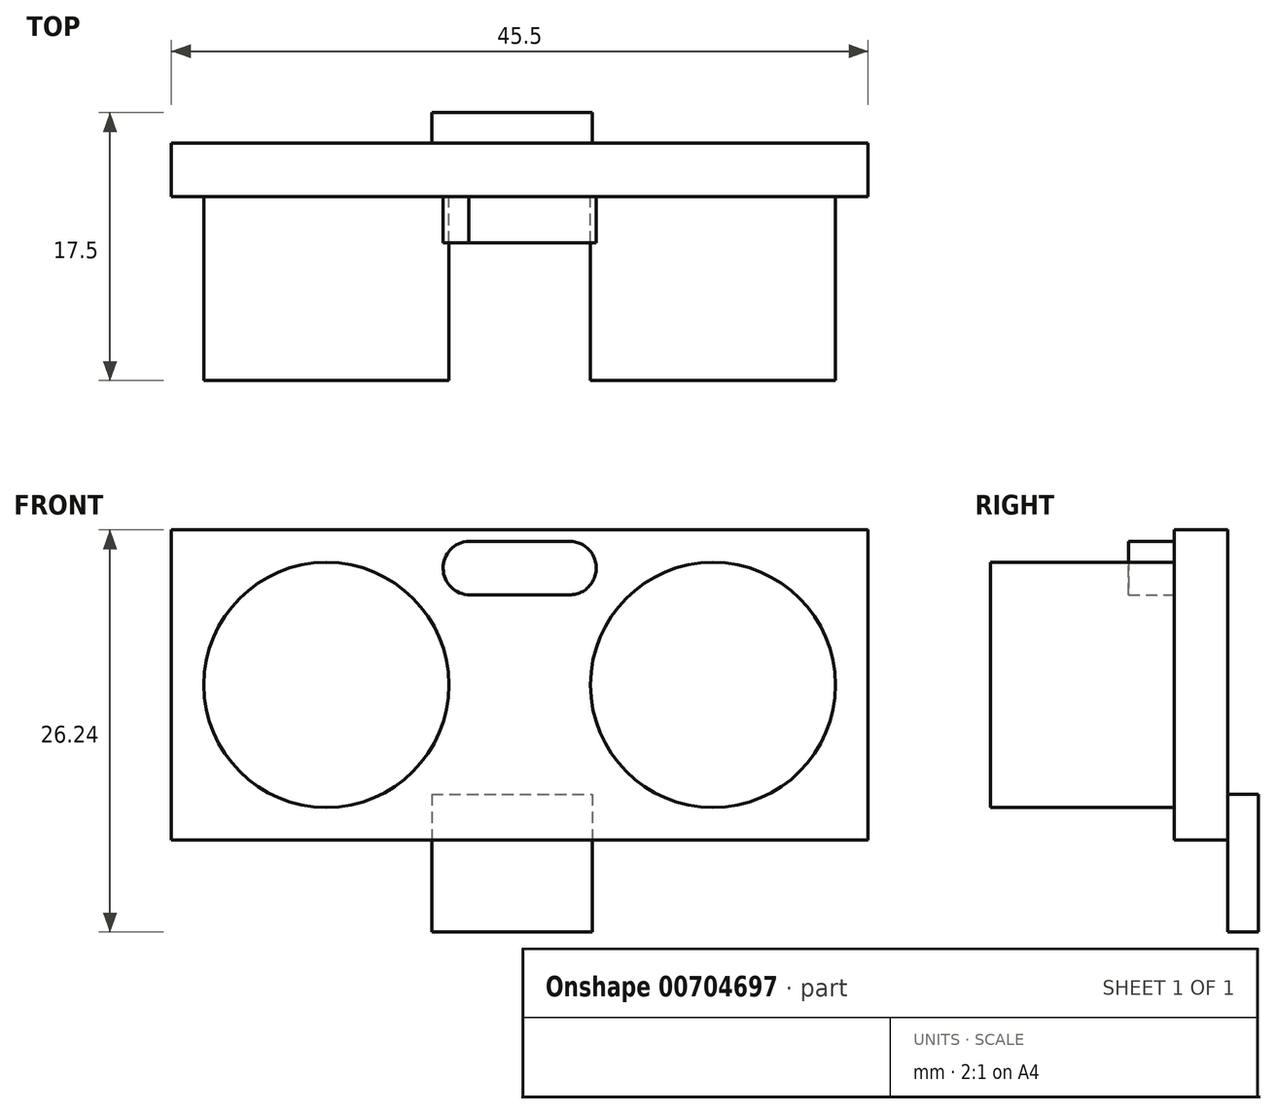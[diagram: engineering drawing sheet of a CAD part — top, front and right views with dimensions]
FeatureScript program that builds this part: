
annotation { "Feature Type Name" : "Feature", "Feature Type Description" : "" }
export const myFeature = defineFeature(function(context is Context, id is Id, definition is map)
    precondition{}
    {
        {
            var Q0;
            Q0=qCreatedBy(makeId("Front.planeOp"),FACE);
            var sketch = newSketch(context, id + "F0", { "sketchPlane" : qUnion([Q0])});
            skLineSegment(sketch, "E0.bottom", {"start": v(-22.75, 10.12) * mm, "end": v(22.75, 10.12) * mm});
            skLineSegment(sketch, "E0.top", {"start": v(-22.75, -10.13) * mm, "end": v(22.75, -10.12) * mm});
            skLineSegment(sketch, "E0.left", {"start": v(-22.75, 10.13) * mm, "end": v(-22.75, -10.12) * mm});
            skLineSegment(sketch, "E0.right", {"start": v(22.75, 10.13) * mm, "end": v(22.75, -10.12) * mm});
            skCircle(sketch, "E1", {"center": v(-12.62, 0) * mm, "radius": 8 * mm});
            skCircle(sketch, "E2", {"center": v(12.62, 0) * mm, "radius": 8 * mm});
            skLineSegment(sketch, "E3.bottom", {"start": v(-5.75, -7.12) * mm, "end": v(4.75, -7.12) * mm});
            skLineSegment(sketch, "E3.top", {"start": v(-5.75, -16.12) * mm, "end": v(4.75, -16.12) * mm});
            skLineSegment(sketch, "E3.left", {"start": v(-5.75, -7.12) * mm, "end": v(-5.75, -16.12) * mm});
            skLineSegment(sketch, "E3.right", {"start": v(4.75, -7.12) * mm, "end": v(4.75, -16.12) * mm});
            skCircle(sketch, "E4", {"center": v(-3.25, 7.63) * mm, "radius": 1.75 * mm});
            skCircle(sketch, "E5", {"center": v(3.25, 7.63) * mm, "radius": 1.75 * mm});
            skLineSegment(sketch, "E6", {"start": v(-3.25, 7.63) * mm, "end": v(3.25, 7.63) * mm});
            skLineSegment(sketch, "E7", {"start": v(-3.32, 9.38) * mm, "end": v(3.25, 9.38) * mm});
            skLineSegment(sketch, "E8", {"start": v(-3.25, 5.88) * mm, "end": v(3.25, 5.88) * mm});
            skSolve(sketch);
        }
        {
            var Q0;
            Q0=makeQuery(id+"F0.imprint","IMPRINT",FACE,{"disambiguationData":[TD([[makeQuery(id+"F0.imprint","IMPRINT",EDGE,{"derivedFrom":sQuery(id+"F0.wireOp",EDGE,"E0.bottom")}),-1.0]])]});
            var Q1;
            Q1=makeQuery(id+"F0.imprint","IMPRINT",FACE,{"disambiguationData":[TD([[makeQuery(id+"F0.imprint","IMPRINT",EDGE,{"derivedFrom":sQuery(id+"F0.wireOp",EDGE,"E1")}),1.0]])]});
            var Q2;
            Q2=makeQuery(id+"F0.imprint","IMPRINT",FACE,{"disambiguationData":[TD([[makeQuery(id+"F0.imprint","IMPRINT",EDGE,{"derivedFrom":sQuery(id+"F0.wireOp",EDGE,"E2")}),1.0]])]});
            var Q3;
            {var subQ5=sQuery(id+"F0.wireOp",EDGE,"E3.bottom");Q3=makeQuery(id+"F0.imprint","IMPRINT",FACE,{"disambiguationData":[TD([[makeQuery(id+"F0.imprint","IMPRINT",EDGE,{"derivedFrom":subQ5}),-1.0]])]});}
            extrude(context, id + "F1", {"entities" : qUnion([Q0, Q1, Q2, Q3]), "depth" : 3.5 * mm, "offsetDistance" : 25 * mm});
        }
        {
            var Q0;
            Q0=makeQuery(id+"F0.imprint","IMPRINT",FACE,{"disambiguationData":[TD([[makeQuery(id+"F0.imprint","IMPRINT",EDGE,{"derivedFrom":sQuery(id+"F0.wireOp",EDGE,"E1")}),1.0]])]});
            var Q1;
            Q1=makeQuery(id+"F0.imprint","IMPRINT",FACE,{"disambiguationData":[TD([[makeQuery(id+"F0.imprint","IMPRINT",EDGE,{"derivedFrom":sQuery(id+"F0.wireOp",EDGE,"E2")}),1.0]])]});
            extrude(context, id + "F2", {"entities" : qUnion([Q0, Q1]), "operationType" : NewBodyOperationType.ADD, "depth" : 15.5 * mm, "offsetDistance" : 25 * mm});
        }
        {
            var Q0;
            {var subQ0=sQuery(id+"F0.wireOp",EDGE,"E6");var subQ1=sQuery(id+"F0.wireOp",EDGE,"E4");var subQ2=makeQuery(id+"F0.imprint","INTERSECT",VERTEX,{"derivedFrom":[subQ1,subQ0]});Q0=makeQuery(id+"F0.imprint","IMPRINT",FACE,{"disambiguationData":[TD([[makeQuery(id+"F0.imprint","IMPRINT",EDGE,{"disambiguationData":[TD([[subQ2,-1.0]])],"derivedFrom":subQ1}),-1.0]])]});}
            var Q1;
            {var subQ3=sQuery(id+"F0.wireOp",EDGE,"E8");Q1=makeQuery(id+"F0.imprint","IMPRINT",FACE,{"disambiguationData":[TD([[makeQuery(id+"F0.imprint","IMPRINT",EDGE,{"derivedFrom":subQ3}),1.0]])]});}
            var Q2;
            {var subQ0=sQuery(id+"F0.wireOp",EDGE,"E4");var subQ1=makeQuery(id+"F0.imprint","INTERSECT",VERTEX,{"derivedFrom":[subQ0,sQuery(id+"F0.wireOp",EDGE,"E6")]});Q2=makeQuery(id+"F0.imprint","IMPRINT",FACE,{"disambiguationData":[TD([[makeQuery(id+"F0.imprint","IMPRINT",EDGE,{"disambiguationData":[TD([[subQ1,1.0]])],"derivedFrom":subQ0}),1.0]])]});}
            var Q3;
            {var subQ0=sQuery(id+"F0.wireOp",EDGE,"E5");var subQ1=makeQuery(id+"F0.imprint","INTERSECT",VERTEX,{"derivedFrom":[subQ0,sQuery(id+"F0.wireOp",EDGE,"E8")]});Q3=makeQuery(id+"F0.imprint","IMPRINT",FACE,{"disambiguationData":[TD([[makeQuery(id+"F0.imprint","IMPRINT",EDGE,{"disambiguationData":[TD([[subQ1,-1.0]])],"derivedFrom":subQ0}),1.0]])]});}
            extrude(context, id + "F3", {"entities" : qUnion([Q0, Q1, Q2, Q3]), "operationType" : NewBodyOperationType.ADD, "depth" : 6.5 * mm, "offsetDistance" : 25 * mm});
        }
        {
            var Q0;
            {var subQ5=sQuery(id+"F0.wireOp",EDGE,"E3.bottom");Q0=makeQuery(id+"F0.imprint","IMPRINT",FACE,{"disambiguationData":[TD([[makeQuery(id+"F0.imprint","IMPRINT",EDGE,{"derivedFrom":subQ5}),-1.0]])]});}
            var Q1;
            {var subQ5=sQuery(id+"F0.wireOp",EDGE,"E3.top");Q1=makeQuery(id+"F0.imprint","IMPRINT",FACE,{"disambiguationData":[TD([[makeQuery(id+"F0.imprint","IMPRINT",EDGE,{"derivedFrom":subQ5}),1.0]])]});}
            extrude(context, id + "F4", {"entities" : qUnion([Q0, Q1]), "operationType" : NewBodyOperationType.ADD, "oppositeDirection" : true, "depth" : 2 * mm, "offsetDistance" : 25 * mm});
        }
    });
